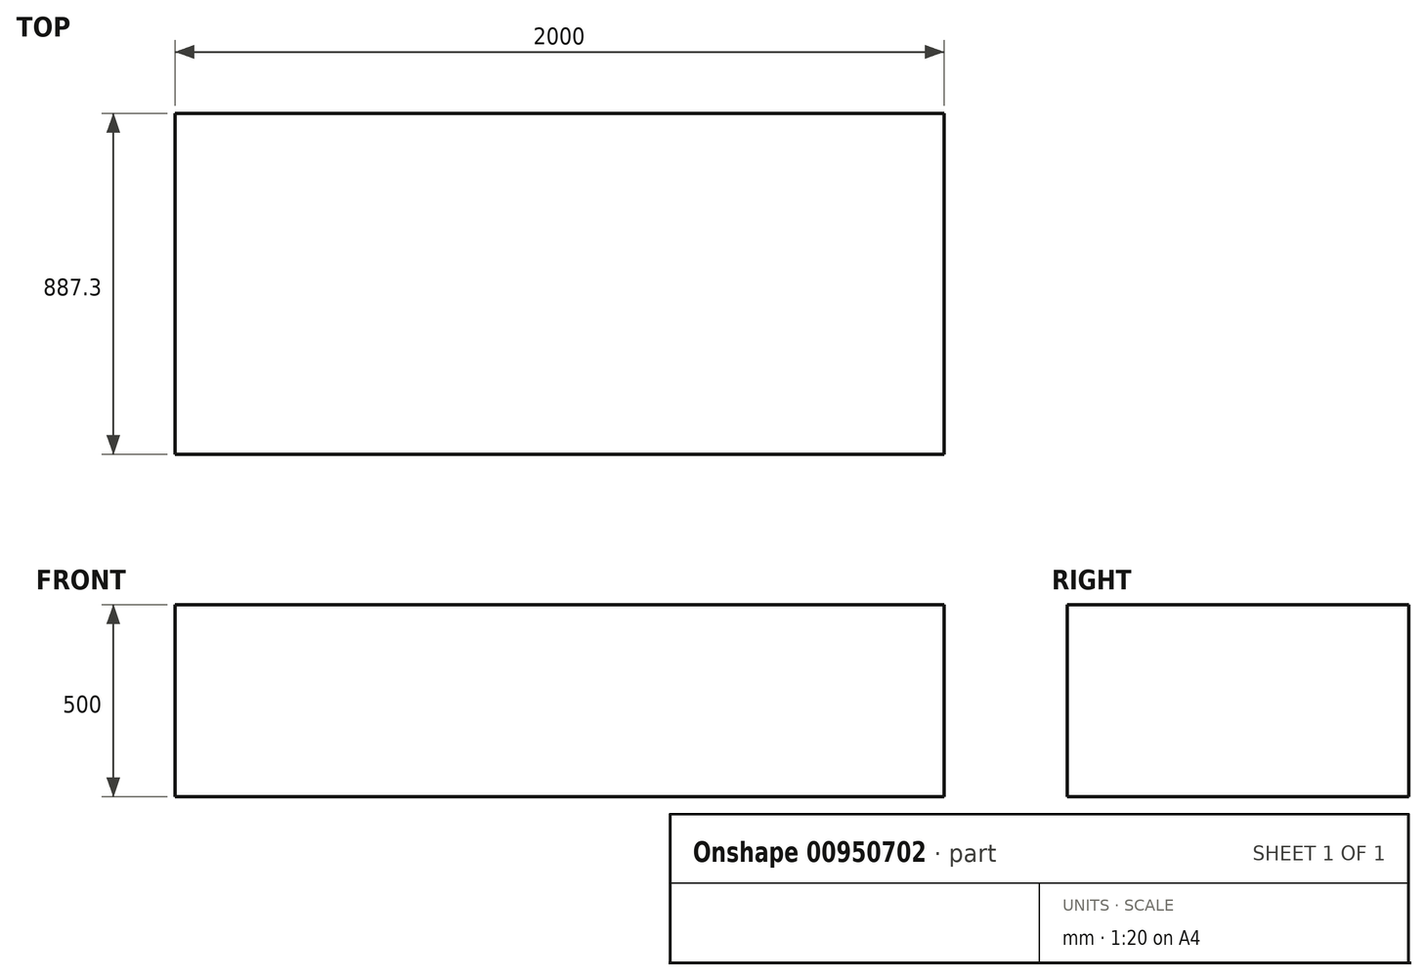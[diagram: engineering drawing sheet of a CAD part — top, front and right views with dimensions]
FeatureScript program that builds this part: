
annotation { "Feature Type Name" : "Feature", "Feature Type Description" : "" }
export const myFeature = defineFeature(function(context is Context, id is Id, definition is map)
    precondition{}
    {
        {
            var Q0;
            Q0=qCreatedBy(makeId("Top.planeOp"),FACE);
            var sketch = newSketch(context, id + "F0", { "sketchPlane" : qUnion([Q0])});
            skLineSegment(sketch, "E0.bottom", {"start": v(-1000, 443.65) * mm, "end": v(1000, 443.65) * mm});
            skLineSegment(sketch, "E0.top", {"start": v(-1000, -443.65) * mm, "end": v(1000, -443.65) * mm});
            skLineSegment(sketch, "E0.left", {"start": v(-1000, 443.65) * mm, "end": v(-1000, -443.65) * mm});
            skLineSegment(sketch, "E0.right", {"start": v(1000, 443.65) * mm, "end": v(1000, -443.65) * mm});
            skPoint(sketch, "E0.middle", {"position": v(0, 0) * mm});
            skSolve(sketch);
        }
        {
            var Q0;
            Q0 = qSketchRegion(id + "F0", true);
            extrude(context, id + "F1", {"entities" : qUnion([Q0]), "depth" : 500 * mm, "offsetDistance" : 25 * mm});
        }
    });
